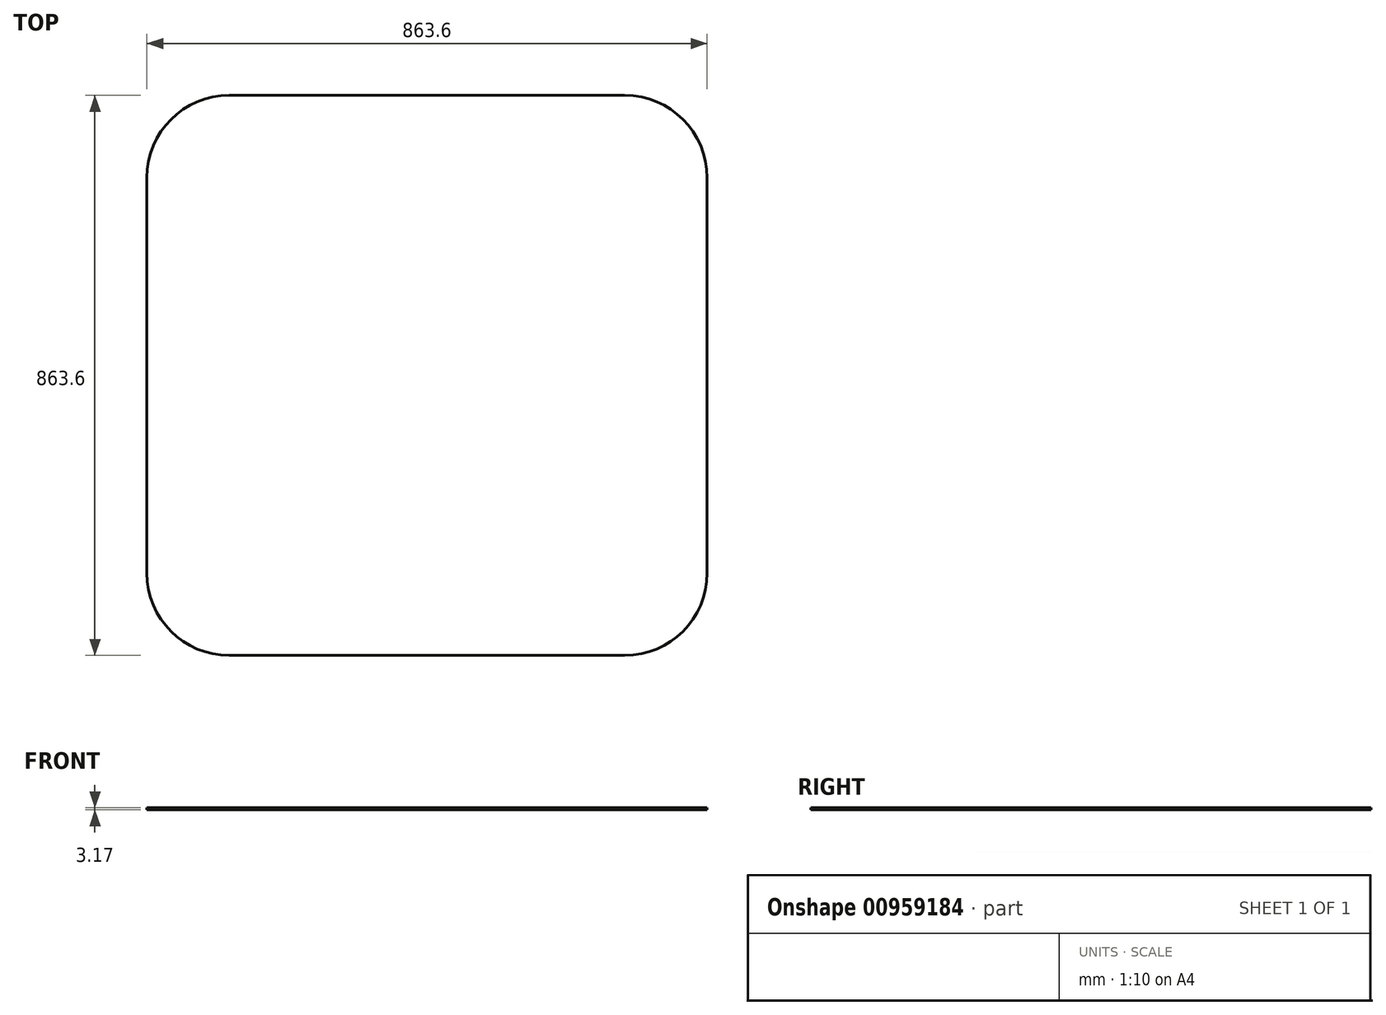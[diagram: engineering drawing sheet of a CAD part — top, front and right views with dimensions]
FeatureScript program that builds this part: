
annotation { "Feature Type Name" : "Feature", "Feature Type Description" : "" }
export const myFeature = defineFeature(function(context is Context, id is Id, definition is map)
    precondition{}
    {
        {
            var Q0;
            Q0=qCreatedBy(makeId("Top.planeOp"),FACE);
            var sketch = newSketch(context, id + "F0", { "sketchPlane" : qUnion([Q0])});
            skLineSegment(sketch, "E0.bottom", {"start": v(-304.8, 431.8) * mm, "end": v(304.8, 431.8) * mm});
            skLineSegment(sketch, "E0.top", {"start": v(-304.8, -431.8) * mm, "end": v(304.8, -431.8) * mm});
            skLineSegment(sketch, "E0.left", {"start": v(-431.8, 304.8) * mm, "end": v(-431.8, -304.8) * mm});
            skLineSegment(sketch, "E0.right", {"start": v(431.8, 304.8) * mm, "end": v(431.8, -304.8) * mm});
            skPoint(sketch, "E0.middle", {"position": v(0, 0) * mm});
            skPoint(sketch, "E1.visualSharp", {"position": v(-431.8, 431.8) * mm});
            skArc(sketch, "E1.filletArc", {"start": v(-304.8, 431.8) * mm, "mid": v(-394.6, 394.6) * mm, "end": v(-431.8, 304.8) * mm});
            skPoint(sketch, "E2.visualSharp", {"position": v(431.8, 431.8) * mm});
            skArc(sketch, "E2.filletArc", {"start": v(431.8, 304.8) * mm, "mid": v(394.6, 394.6) * mm, "end": v(304.8, 431.8) * mm});
            skPoint(sketch, "E3.visualSharp", {"position": v(431.8, -431.8) * mm});
            skArc(sketch, "E3.filletArc", {"start": v(304.8, -431.8) * mm, "mid": v(394.6, -394.6) * mm, "end": v(431.8, -304.8) * mm});
            skPoint(sketch, "E4.visualSharp", {"position": v(-431.8, -431.8) * mm});
            skArc(sketch, "E4.filletArc", {"start": v(-431.8, -304.8) * mm, "mid": v(-394.6, -394.6) * mm, "end": v(-304.8, -431.8) * mm});
            skSolve(sketch);
        }
        {
            var Q0;
            Q0 = qSketchRegion(id + "F0", true);
            extrude(context, id + "F1", {"entities" : qUnion([Q0]), "depth" : 3.17 * mm, "offsetDistance" : 25.4 * mm});
        }
    });
